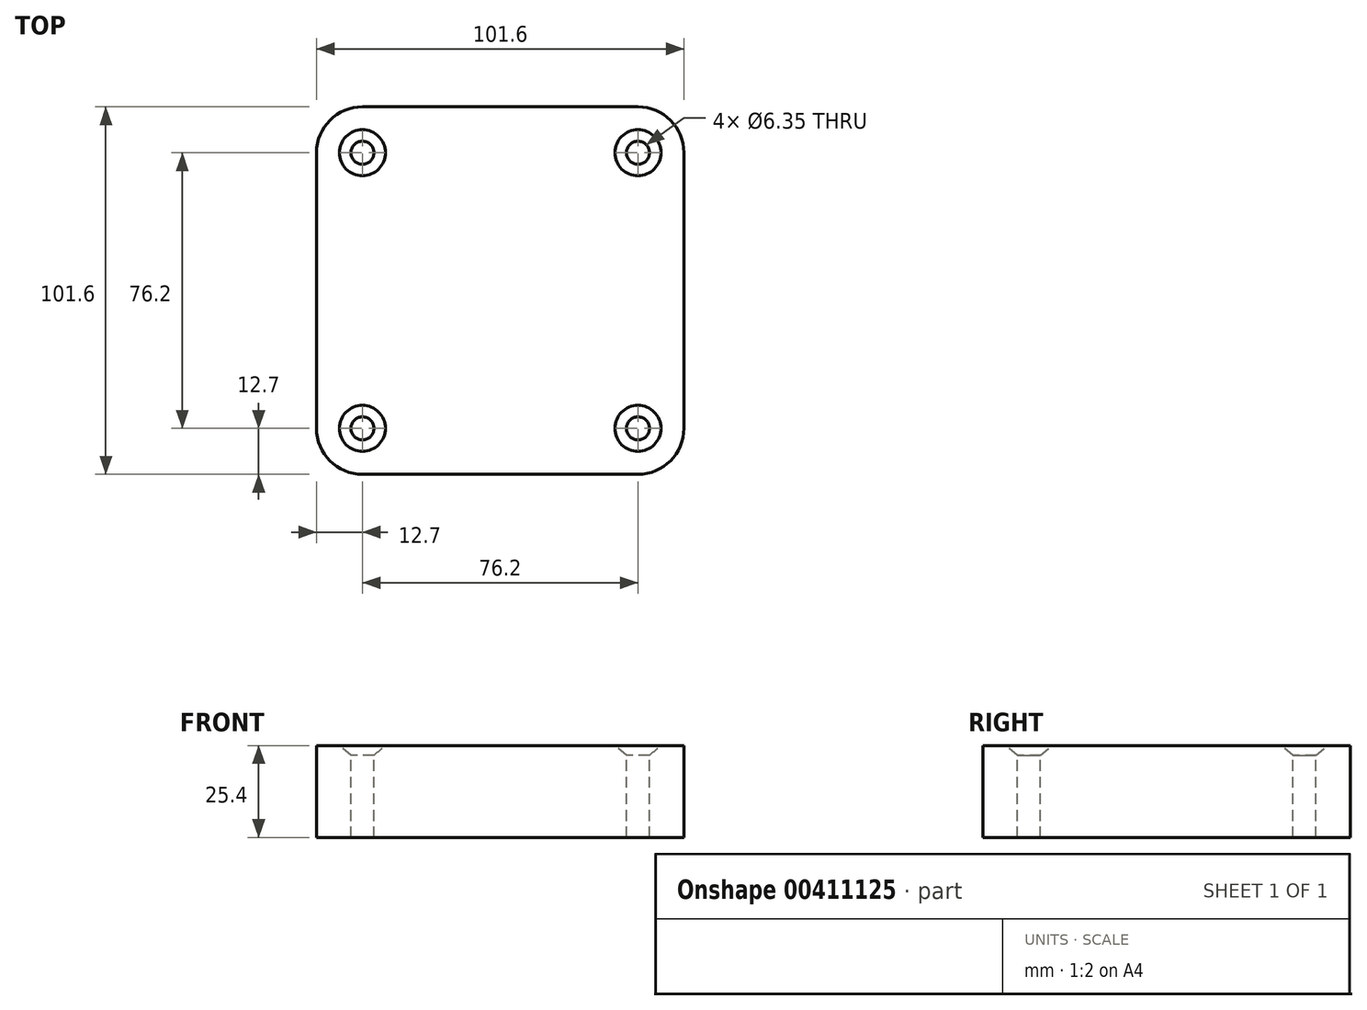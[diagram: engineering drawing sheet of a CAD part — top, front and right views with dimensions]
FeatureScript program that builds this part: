
annotation { "Feature Type Name" : "Feature", "Feature Type Description" : "" }
export const myFeature = defineFeature(function(context is Context, id is Id, definition is map)
    precondition{}
    {
        {
            var Q0;
            Q0=qCreatedBy(makeId("Top.planeOp"),FACE);
            var sketch = newSketch(context, id + "F0", { "sketchPlane" : qUnion([Q0])});
            skLineSegment(sketch, "E0.bottom", {"start": v(-38.1, -50.8) * mm, "end": v(38.1, -50.8) * mm});
            skLineSegment(sketch, "E0.top", {"start": v(-38.1, 50.8) * mm, "end": v(38.1, 50.8) * mm});
            skLineSegment(sketch, "E0.left", {"start": v(-50.8, -38.1) * mm, "end": v(-50.8, 38.1) * mm});
            skLineSegment(sketch, "E0.right", {"start": v(50.8, -38.1) * mm, "end": v(50.8, 38.1) * mm});
            skPoint(sketch, "E0.middle", {"position": v(0, 0) * mm});
            skPoint(sketch, "E1.visualSharp", {"position": v(-50.8, 50.8) * mm});
            skArc(sketch, "E1.filletArc", {"start": v(-38.1, 50.8) * mm, "mid": v(-47.08, 47.08) * mm, "end": v(-50.8, 38.1) * mm});
            skPoint(sketch, "E2.visualSharp", {"position": v(50.8, 50.8) * mm});
            skArc(sketch, "E2.filletArc", {"start": v(50.8, 38.1) * mm, "mid": v(47.08, 47.08) * mm, "end": v(38.1, 50.8) * mm});
            skPoint(sketch, "E3.visualSharp", {"position": v(50.8, -50.8) * mm});
            skArc(sketch, "E3.filletArc", {"start": v(38.1, -50.8) * mm, "mid": v(47.08, -47.08) * mm, "end": v(50.8, -38.1) * mm});
            skPoint(sketch, "E4.visualSharp", {"position": v(-50.8, -50.8) * mm});
            skArc(sketch, "E4.filletArc", {"start": v(-50.8, -38.1) * mm, "mid": v(-47.08, -47.08) * mm, "end": v(-38.1, -50.8) * mm});
            skSolve(sketch);
        }
        {
            var Q0;
            Q0=makeQuery(id+"F0.imprint","IMPRINT",FACE,{"disambiguationData":[TD([[makeQuery(id+"F0.imprint","IMPRINT",EDGE,{"derivedFrom":sQuery(id+"F0.wireOp",EDGE,"E0.bottom")}),1.0]])]});
            extrude(context, id + "F1", {"entities" : qUnion([Q0]), "depth" : 25.4 * mm});
        }
        {
            var Q0;
            Q0=makeQuery(id+"F1.opExtrude","CAP_FACE",FACE,{"disambiguationData":[OSD([sQuery(id+"F0.wireOp",EDGE,"E0.bottom"),sQuery(id+"F0.wireOp",EDGE,"E0.top"),sQuery(id+"F0.wireOp",EDGE,"E0.left"),sQuery(id+"F0.wireOp",EDGE,"E0.right"),sQuery(id+"F0.wireOp",EDGE,"E1.filletArc"),sQuery(id+"F0.wireOp",EDGE,"E2.filletArc"),sQuery(id+"F0.wireOp",EDGE,"E3.filletArc"),sQuery(id+"F0.wireOp",EDGE,"E4.filletArc")])],"isStart":false});
            var sketch = newSketch(context, id + "F2", { "sketchPlane" : qUnion([Q0])});
            skPoint(sketch, "E5", {"position": v(-38.1, 38.1) * mm});
            skPoint(sketch, "E6", {"position": v(38.1, 38.1) * mm});
            skPoint(sketch, "E7", {"position": v(38.1, -38.1) * mm});
            skPoint(sketch, "E8", {"position": v(-38.1, -38.1) * mm});
            skSolve(sketch);
        }
        {
            var Q0;
            Q0=sQuery(id+"F2.wireOp",VERTEX,"E5");
            var Q1;
            Q1=sQuery(id+"F2.wireOp",VERTEX,"E6");
            var Q2;
            Q2=sQuery(id+"F2.wireOp",VERTEX,"E7");
            var Q3;
            Q3=sQuery(id+"F2.wireOp",VERTEX,"E8");
            var Q4;
            Q4=makeQuery(id+"F1.opExtrude","SWEPT_BODY",BODY,{"disambiguationData":[OSD([sQuery(id+"F0.wireOp",EDGE,"E0.bottom"),sQuery(id+"F0.wireOp",EDGE,"E0.top"),sQuery(id+"F0.wireOp",EDGE,"E0.left"),sQuery(id+"F0.wireOp",EDGE,"E0.right"),sQuery(id+"F0.wireOp",EDGE,"E1.filletArc"),sQuery(id+"F0.wireOp",EDGE,"E2.filletArc"),sQuery(id+"F0.wireOp",EDGE,"E3.filletArc"),sQuery(id+"F0.wireOp",EDGE,"E4.filletArc")])]});
            hole(context, id + "F3", {"style" : HoleStyle.C_SINK, "endStyle" : HoleEndStyle.THROUGH, "holeDiameter" : 6.35 * mm, "cSinkDiameter" : 12.7 * mm, "cSinkAngle" : 100 * degree, "isTappedThrough" : true, "tappedDepth" : 12.7 * mm, "tapClearance" : 3, "locations" : qUnion([Q0, Q1, Q2, Q3]), "scope" : qUnion([Q4])});
        }
    });
